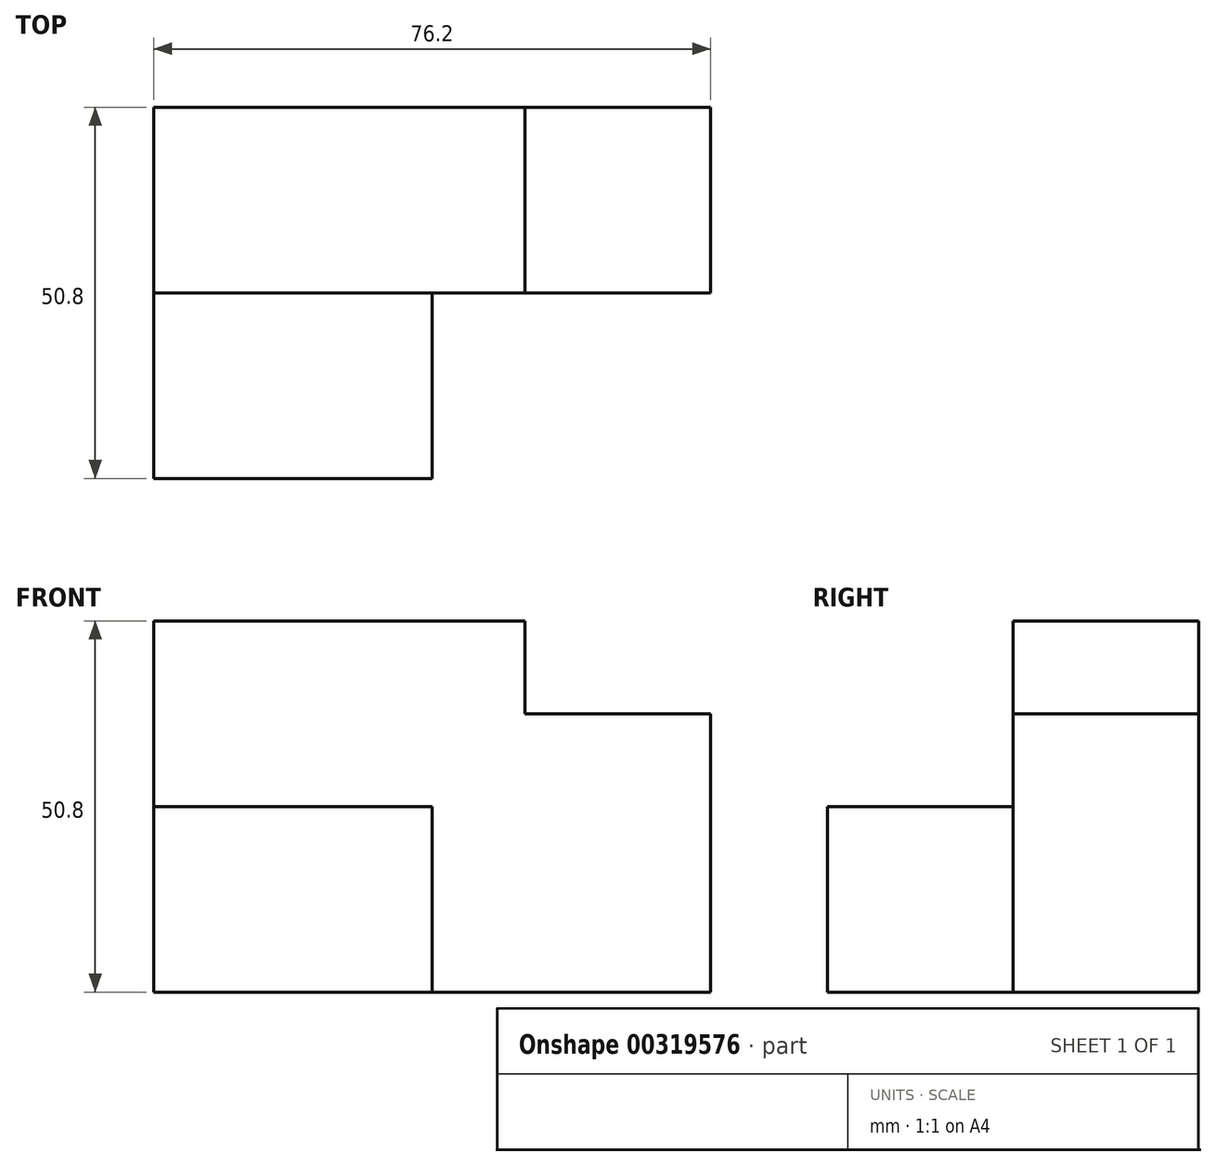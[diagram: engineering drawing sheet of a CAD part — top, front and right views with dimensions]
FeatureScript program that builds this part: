
annotation { "Feature Type Name" : "Feature", "Feature Type Description" : "" }
export const myFeature = defineFeature(function(context is Context, id is Id, definition is map)
    precondition{}
    {
        {
            var Q0;
            Q0=qCreatedBy(makeId("Front.planeOp"),FACE);
            var sketch = newSketch(context, id + "F0", { "sketchPlane" : qUnion([Q0])});
            skLineSegment(sketch, "E0", {"start": v(-35.78, -52.8) * mm, "end": v(40.42, -52.8) * mm});
            skLineSegment(sketch, "E1", {"start": v(40.42, -52.8) * mm, "end": v(40.42, -2) * mm});
            skLineSegment(sketch, "E2", {"start": v(40.42, -2) * mm, "end": v(-35.78, -2) * mm});
            skLineSegment(sketch, "E3", {"start": v(-35.78, -2) * mm, "end": v(-35.78, -52.8) * mm});
            skSolve(sketch);
        }
        {
            var Q0;
            Q0=makeQuery(id+"F0.imprint","IMPRINT",FACE,{"disambiguationData":[TD([[makeQuery(id+"F0.imprint","IMPRINT",EDGE,{"derivedFrom":sQuery(id+"F0.wireOp",EDGE,"E0")}),1.0]])]});
            extrude(context, id + "F1", {"entities" : qUnion([Q0]), "depth" : 25.4 * mm});
        }
        {
            var Q0;
            Q0=makeQuery(id+"F1.opExtrude","SWEPT_FACE",FACE,{"disambiguationData":[OSD([sQuery(id+"F0.wireOp",EDGE,"E2")])]});
            var sketch = newSketch(context, id + "F2", { "sketchPlane" : qUnion([Q0])});
            skLineSegment(sketch, "E4", {"start": v(15.02, -25.4) * mm, "end": v(40.42, -25.4) * mm});
            skLineSegment(sketch, "E5", {"start": v(40.42, -25.4) * mm, "end": v(40.42, 0) * mm});
            skLineSegment(sketch, "E6", {"start": v(40.42, 0) * mm, "end": v(15.02, 0) * mm});
            skLineSegment(sketch, "E7", {"start": v(15.02, 0) * mm, "end": v(15.02, -25.4) * mm});
            skSolve(sketch);
        }
        {
            var Q0;
            Q0=makeQuery(id+"F2.imprint","IMPRINT",FACE,{"disambiguationData":[TD([[makeQuery(id+"F2.imprint","IMPRINT",EDGE,{"derivedFrom":sQuery(id+"F2.wireOp",EDGE,"E4")}),-1.0]])]});
            extrude(context, id + "F3", {"entities" : qUnion([Q0]), "operationType" : NewBodyOperationType.REMOVE, "oppositeDirection" : true, "depth" : 12.7 * mm});
        }
        {
            var Q0;
            Q0=makeQuery(id+"F1.opExtrude","CAP_FACE",FACE,{"disambiguationData":[OSD([sQuery(id+"F0.wireOp",EDGE,"E0"),sQuery(id+"F0.wireOp",EDGE,"E1"),sQuery(id+"F0.wireOp",EDGE,"E2"),sQuery(id+"F0.wireOp",EDGE,"E3")])],"isStart":false});
            var sketch = newSketch(context, id + "F4", { "sketchPlane" : qUnion([Q0])});
            skLineSegment(sketch, "E8", {"start": v(-35.78, -52.8) * mm, "end": v(2.32, -52.8) * mm});
            skLineSegment(sketch, "E9", {"start": v(2.32, -52.8) * mm, "end": v(2.32, -27.4) * mm});
            skLineSegment(sketch, "E10", {"start": v(2.32, -27.4) * mm, "end": v(-35.78, -27.4) * mm});
            skLineSegment(sketch, "E11", {"start": v(-35.78, -27.4) * mm, "end": v(-35.78, -52.8) * mm});
            skSolve(sketch);
        }
        {
            var Q0;
            Q0=makeQuery(id+"F4.imprint","IMPRINT",FACE,{"disambiguationData":[TD([[makeQuery(id+"F4.imprint","IMPRINT",EDGE,{"derivedFrom":sQuery(id+"F4.wireOp",EDGE,"E8")}),1.0]])]});
            extrude(context, id + "F5", {"entities" : qUnion([Q0]), "operationType" : NewBodyOperationType.ADD, "depth" : 25.4 * mm});
        }
    });
